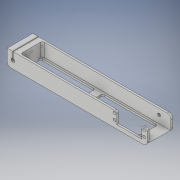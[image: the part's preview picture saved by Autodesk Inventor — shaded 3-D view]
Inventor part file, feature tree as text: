
AUTODESK INVENTOR PART (.ipt)
format: ipt  version: 2017 (Build 210142000, 142)  size: 309,248 bytes
history: native  units: in
note: dims shown in document units (in); Inventor stores cm internally (conversion verified against a paired STEP export)
features: sketch x7, projected_geometry x6, extrude x5, fillet x4, hole x3
ambient origin geometry x8: Origin, YZ Plane, XZ Plane, XY Plane, X Axis, Y Axis, Z Axis, Center Point
bodies: Solid1 (feature_tree)
feature tree (25):
  extrude  "Extrusion1"  Depth=1.685in
  extrude  "Extrusion2"  Depth=1.435in
  extrude  "Extrusion4"  Depth=0.125in TaperAngle=0.0deg
  extrude  "Extrusion5"  Depth=1.0in
  hole  "Hole1"  [1 undecoded]
  hole  "Hole2"  [1 undecoded]
  fillet  "Fillet1"  Radius=0.164in
  hole  "Hole3"  [1 undecoded]
  fillet  "Fillet2"  Radius=0.19in
  fillet  "Fillet3"  Radius=0.5in
  extrude  "Extrusion6"  Depth=0.125in
  fillet  "Fillet4"  Radius=0.361in
  sketch  "Sketch1"  dims[d0=1.0in d1=1.685in]
  sketch  "Sketch2"  dims[d2=0.875in d3=1.435in]
  projected_geometry  "Projected Loop1"
  projected_geometry  "Projected Loop2"
  sketch  "Sketch4"  dims[d4=0.125in d5=9.197in d6=0.0in]
  projected_geometry  "Projected Loop3"
  sketch  "Sketch5"  dims[d7=0.35in d8=1.0in]
  sketch  "Sketch6"  dims[d9=0.75in d10=2.0in]
  projected_geometry  "Projected Loop4"
  sketch  "Sketch7"  dims[d11=0.19in d12=0.19in d13=0.164in]
  projected_geometry  "Projected Loop5"
  sketch  "Sketch9"  dims[d14=0.3937in d15=0.19in d16=0.19in d19=0.5in d20=0.0in d22=0.776in d23=0.361in d26=0.75in d27=0.133in d28=0.078in d29=0.078in d30=0.098in d31=0.236in d32=0.0665in d33=0.0665in d34=0.0665in d35=0.0in d36=0.118in d37=0.133in d38=1.0in d39=0.5in d40=0.375in d41=0.05in d42=0.35in d43=1.685in d44=0.0in d45=0.75in d46=0.078in d47=0.078in d48=0.098in d49=0.0665in d50=0.0665in d51=0.0665in d52=0.0in d53=0.133in d54=1.0in d55=0.5in d56=0.375in d57=0.35in d58=0.133in d59=0.05in d60=1.685in d61=0.0in d62=0.25in d63=0.25in d64=1.685in d65=0.25in d66=0.8425in d67=0.2106in d68=0.2106in d69=0.158in d70=0.75in d71=0.375in d72=0.25in d73=0.5635in d74=0.355in d75=0.8108in d76=0.104in d77=0.276in d78=0.375in d79=0.25in d80=0.5635in d81=0.432in d82=0.8108in d83=0.125in d84=0.196in d85=0.5in d86=0.375in d87=0.25in d88=0.5635in d89=0.75in d90=0.8108in d91=1.9488in d92=1.9488in d93=0.164in d95=0.3937in d96=0.197in d97=0.197in d105=0.25in d106=0.125in d107=1.685in d108=8.697in d109=0.5in d110=0.25in d111=1.185in d112=3.5985in d113=1.0in d114=0.0in d115=0.5in d116=3.5985in d117=1.185in d118=0.25in d119=0.125in]
  projected_geometry  "Projected Loop7"
note: 3 required parameter values undecoded (feature->parameter linkage not recoverable at this tier; creation-order binding heuristic only, values carry confidence <= 0.55)
